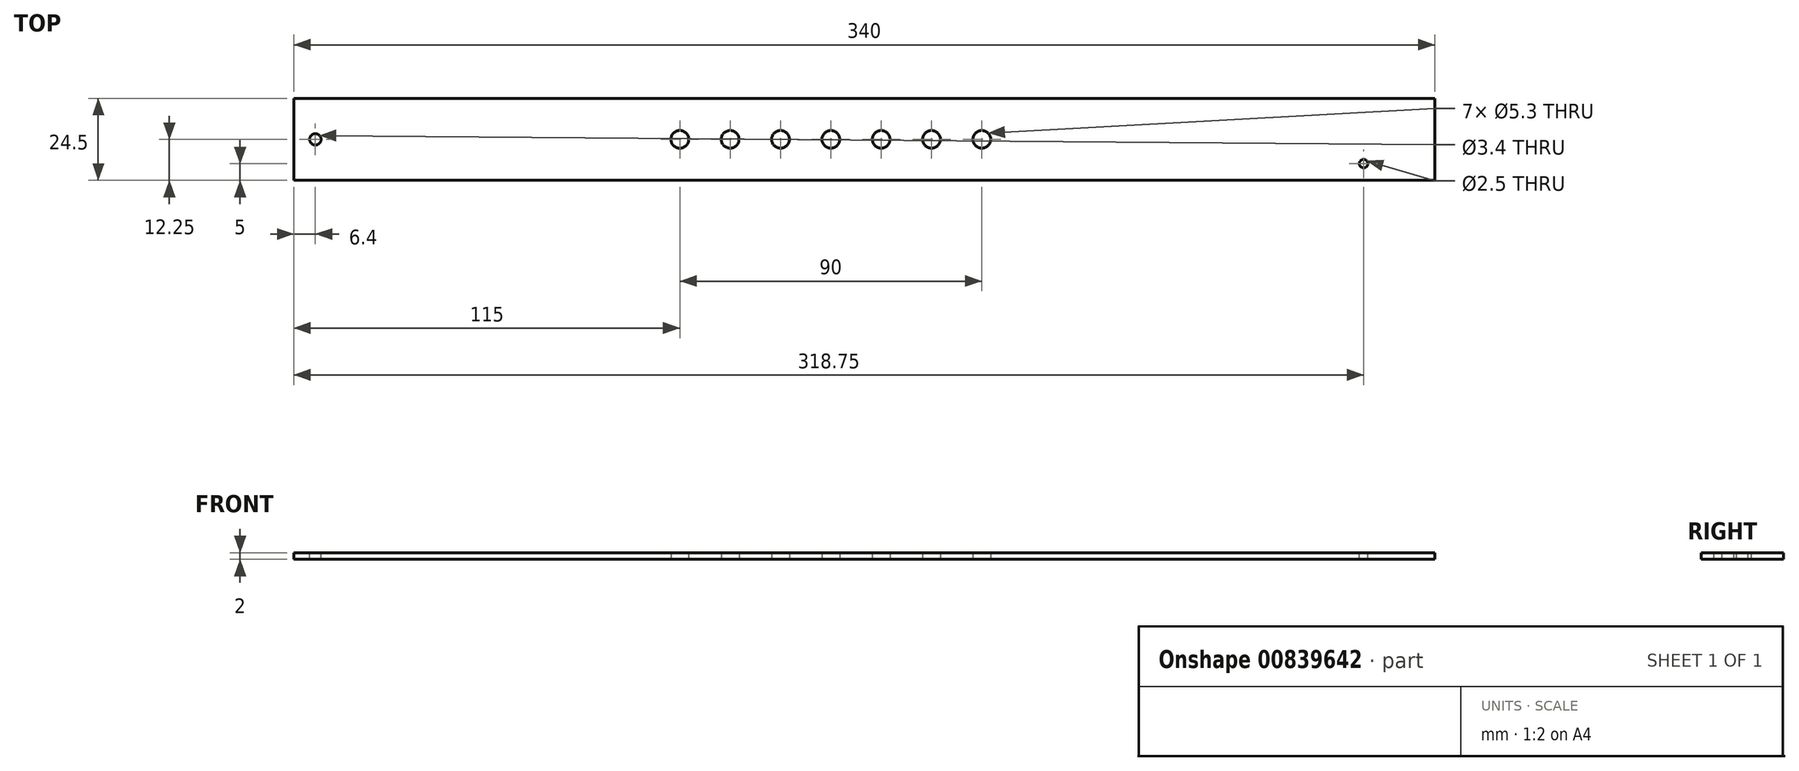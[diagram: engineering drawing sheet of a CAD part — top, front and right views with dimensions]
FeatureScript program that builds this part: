
annotation { "Feature Type Name" : "Feature", "Feature Type Description" : "" }
export const myFeature = defineFeature(function(context is Context, id is Id, definition is map)
    precondition{}
    {
        {
            var Q0;
            Q0=qCreatedBy(makeId("Top.planeOp"),FACE);
            var sketch = newSketch(context, id + "F0", { "sketchPlane" : qUnion([Q0])});
            skLineSegment(sketch, "E0.bottom", {"start": v(150, -12.25) * mm, "end": v(-150, -12.25) * mm});
            skLineSegment(sketch, "E0.top", {"start": v(150, 12.25) * mm, "end": v(-150, 12.25) * mm});
            skLineSegment(sketch, "E0.left", {"start": v(150, -12.25) * mm, "end": v(150, 12.25) * mm});
            skLineSegment(sketch, "E0.right", {"start": v(-150, -12.25) * mm, "end": v(-150, 12.25) * mm});
            skPoint(sketch, "E0.middle", {"position": v(0, 0) * mm});
            skCircle(sketch, "E1.6.0.0", {"center": v(-45, 0) * mm, "radius": 2.65 * mm});
            skCircle(sketch, "E1.7.0.0", {"center": v(-30, 0) * mm, "radius": 2.65 * mm});
            skCircle(sketch, "E1.8.0.0", {"center": v(-15, 0) * mm, "radius": 2.65 * mm});
            skCircle(sketch, "E1.9.0.0", {"center": v(0, 0) * mm, "radius": 2.65 * mm});
            skCircle(sketch, "E1.10.0.0", {"center": v(15, 0) * mm, "radius": 2.65 * mm});
            skCircle(sketch, "E1.11.0.0", {"center": v(30, 0) * mm, "radius": 2.65 * mm});
            skCircle(sketch, "E1.12.0.0", {"center": v(45, 0) * mm, "radius": 2.65 * mm});
            skLineSegment(sketch, "E1.direction1", {"start": v(-135, 0) * mm, "end": v(-120, 0) * mm, "construction": true});
            skSolve(sketch);
        }
        {
            var Q0;
            Q0=makeQuery(id+"F0.imprint","IMPRINT",FACE,{"disambiguationData":[TD([[makeQuery(id+"F0.imprint","IMPRINT",EDGE,{"derivedFrom":sQuery(id+"F0.wireOp",EDGE,"E0.bottom")}),-1.0]])]});
            extrude(context, id + "F1", {"entities" : qUnion([Q0]), "depth" : 2 * mm, "offsetDistance" : 25 * mm});
        }
        {
            var Q0;
            Q0=makeQuery(id+"F1.opExtrude","SWEPT_FACE",FACE,{"disambiguationData":[OSD([sQuery(id+"F0.wireOp",EDGE,"E0.right")])]});
            extrude(context, id + "F2", {"entities" : qUnion([Q0]), "operationType" : NewBodyOperationType.ADD, "depth" : 10 * mm, "offsetDistance" : 25 * mm});
        }
        {
            var Q0;
            Q0=makeQuery(id+"F1.opExtrude","SWEPT_FACE",FACE,{"disambiguationData":[OSD([sQuery(id+"F0.wireOp",EDGE,"E0.left")])]});
            extrude(context, id + "F3", {"entities" : qUnion([Q0]), "operationType" : NewBodyOperationType.ADD, "depth" : 30 * mm, "offsetDistance" : 25 * mm});
        }
        {
            var Q0;
            {var subQ0=sQuery(id+"F0.wireOp",EDGE,"E0.left");var subQ1=sQuery(id+"F0.wireOp",EDGE,"E0.right");Q0=makeQuery(id+"F3.boolean.opBoolean","MERGE",FACE,{"derivedFrom":[makeQuery(id+"F2.boolean.opBoolean","MERGE",FACE,{"derivedFrom":[makeQuery(id+"F1.opExtrude","CAP_FACE",FACE,{"disambiguationData":[OSD([sQuery(id+"F0.wireOp",EDGE,"E0.bottom"),sQuery(id+"F0.wireOp",EDGE,"E0.top"),subQ0,subQ1,sQuery(id+"F0.wireOp",EDGE,"LckrCdrf-Oz9b-iWqB-HkfW-gHpTPrbceAxr"),sQuery(id+"F0.wireOp",EDGE,"E1.1.0.0"),sQuery(id+"F0.wireOp",EDGE,"E1.2.0.0"),sQuery(id+"F0.wireOp",EDGE,"E1.3.0.0"),sQuery(id+"F0.wireOp",EDGE,"E1.4.0.0"),sQuery(id+"F0.wireOp",EDGE,"E1.5.0.0"),sQuery(id+"F0.wireOp",EDGE,"E1.6.0.0"),sQuery(id+"F0.wireOp",EDGE,"E1.7.0.0"),sQuery(id+"F0.wireOp",EDGE,"E1.8.0.0"),sQuery(id+"F0.wireOp",EDGE,"E1.9.0.0"),sQuery(id+"F0.wireOp",EDGE,"E1.10.0.0"),sQuery(id+"F0.wireOp",EDGE,"E1.11.0.0"),sQuery(id+"F0.wireOp",EDGE,"E1.12.0.0"),sQuery(id+"F0.wireOp",EDGE,"E1.13.0.0"),sQuery(id+"F0.wireOp",EDGE,"E1.14.0.0"),sQuery(id+"F0.wireOp",EDGE,"E1.15.0.0"),sQuery(id+"F0.wireOp",EDGE,"E1.16.0.0"),sQuery(id+"F0.wireOp",EDGE,"E1.17.0.0"),sQuery(id+"F0.wireOp",EDGE,"E1.18.0.0")])],"isStart":false}),makeQuery(id+"F2.opExtrude","SWEPT_FACE",FACE,{"disambiguationData":[OSD([subQ1]),TDD([makeQuery(id+"F1.opExtrude","CAP_EDGE",EDGE,{"disambiguationData":[OSD([subQ1])],"isStart":false})])]})]}),makeQuery(id+"F3.opExtrude","SWEPT_FACE",FACE,{"disambiguationData":[OSD([subQ0]),TDD([makeQuery(id+"F1.opExtrude","CAP_EDGE",EDGE,{"disambiguationData":[OSD([subQ0])],"isStart":false})])]})]});}
            var sketch = newSketch(context, id + "F4", { "sketchPlane" : qUnion([Q0])});
            skCircle(sketch, "E2", {"center": v(-153.6, 0) * mm, "radius": 1.7 * mm});
            skSolve(sketch);
        }
        {
            var Q0;
            Q0=makeQuery(id+"F4.imprint","IMPRINT",FACE,{"disambiguationData":[TD([[makeQuery(id+"F4.imprint","IMPRINT",EDGE,{"derivedFrom":sQuery(id+"F4.wireOp",EDGE,"E2")}),1.0]])]});
            extrude(context, id + "F5", {"entities" : qUnion([Q0]), "operationType" : NewBodyOperationType.REMOVE, "endBound" : BoundingType.UP_TO_NEXT, "oppositeDirection" : true, "depth" : 25 * mm, "offsetDistance" : 25 * mm});
        }
        {
            var Q0;
            {var subQ0=sQuery(id+"F0.wireOp",EDGE,"E0.left");var subQ1=sQuery(id+"F0.wireOp",EDGE,"E0.right");Q0=makeQuery(id+"F3.boolean.opBoolean","MERGE",FACE,{"derivedFrom":[makeQuery(id+"F2.boolean.opBoolean","MERGE",FACE,{"derivedFrom":[makeQuery(id+"F1.opExtrude","CAP_FACE",FACE,{"disambiguationData":[OSD([sQuery(id+"F0.wireOp",EDGE,"E0.bottom"),sQuery(id+"F0.wireOp",EDGE,"E0.top"),subQ0,subQ1,sQuery(id+"F0.wireOp",EDGE,"LckrCdrf-Oz9b-iWqB-HkfW-gHpTPrbceAxr"),sQuery(id+"F0.wireOp",EDGE,"E1.1.0.0"),sQuery(id+"F0.wireOp",EDGE,"E1.2.0.0"),sQuery(id+"F0.wireOp",EDGE,"E1.3.0.0"),sQuery(id+"F0.wireOp",EDGE,"E1.4.0.0"),sQuery(id+"F0.wireOp",EDGE,"E1.5.0.0"),sQuery(id+"F0.wireOp",EDGE,"E1.6.0.0"),sQuery(id+"F0.wireOp",EDGE,"E1.7.0.0"),sQuery(id+"F0.wireOp",EDGE,"E1.8.0.0"),sQuery(id+"F0.wireOp",EDGE,"E1.9.0.0"),sQuery(id+"F0.wireOp",EDGE,"E1.10.0.0"),sQuery(id+"F0.wireOp",EDGE,"E1.11.0.0"),sQuery(id+"F0.wireOp",EDGE,"E1.12.0.0"),sQuery(id+"F0.wireOp",EDGE,"E1.13.0.0"),sQuery(id+"F0.wireOp",EDGE,"E1.14.0.0"),sQuery(id+"F0.wireOp",EDGE,"E1.15.0.0"),sQuery(id+"F0.wireOp",EDGE,"E1.16.0.0"),sQuery(id+"F0.wireOp",EDGE,"E1.17.0.0"),sQuery(id+"F0.wireOp",EDGE,"E1.18.0.0")])],"isStart":false}),makeQuery(id+"F2.opExtrude","SWEPT_FACE",FACE,{"disambiguationData":[OSD([subQ1]),TDD([makeQuery(id+"F1.opExtrude","CAP_EDGE",EDGE,{"disambiguationData":[OSD([subQ1])],"isStart":false})])]})]}),makeQuery(id+"F3.opExtrude","SWEPT_FACE",FACE,{"disambiguationData":[OSD([subQ0]),TDD([makeQuery(id+"F1.opExtrude","CAP_EDGE",EDGE,{"disambiguationData":[OSD([subQ0])],"isStart":false})])]})]});}
            var sketch = newSketch(context, id + "F6", { "sketchPlane" : qUnion([Q0])});
            skCircle(sketch, "E3", {"center": v(158.75, -7.25) * mm, "radius": 1.25 * mm});
            skSolve(sketch);
        }
        {
            var Q0;
            Q0=makeQuery(id+"F6.imprint","IMPRINT",FACE,{"disambiguationData":[TD([[makeQuery(id+"F6.imprint","IMPRINT",EDGE,{"derivedFrom":sQuery(id+"F6.wireOp",EDGE,"E3")}),1.0]])]});
            extrude(context, id + "F7", {"entities" : qUnion([Q0]), "operationType" : NewBodyOperationType.REMOVE, "endBound" : BoundingType.UP_TO_NEXT, "oppositeDirection" : true, "depth" : 25 * mm, "offsetDistance" : 25 * mm});
        }
    });
